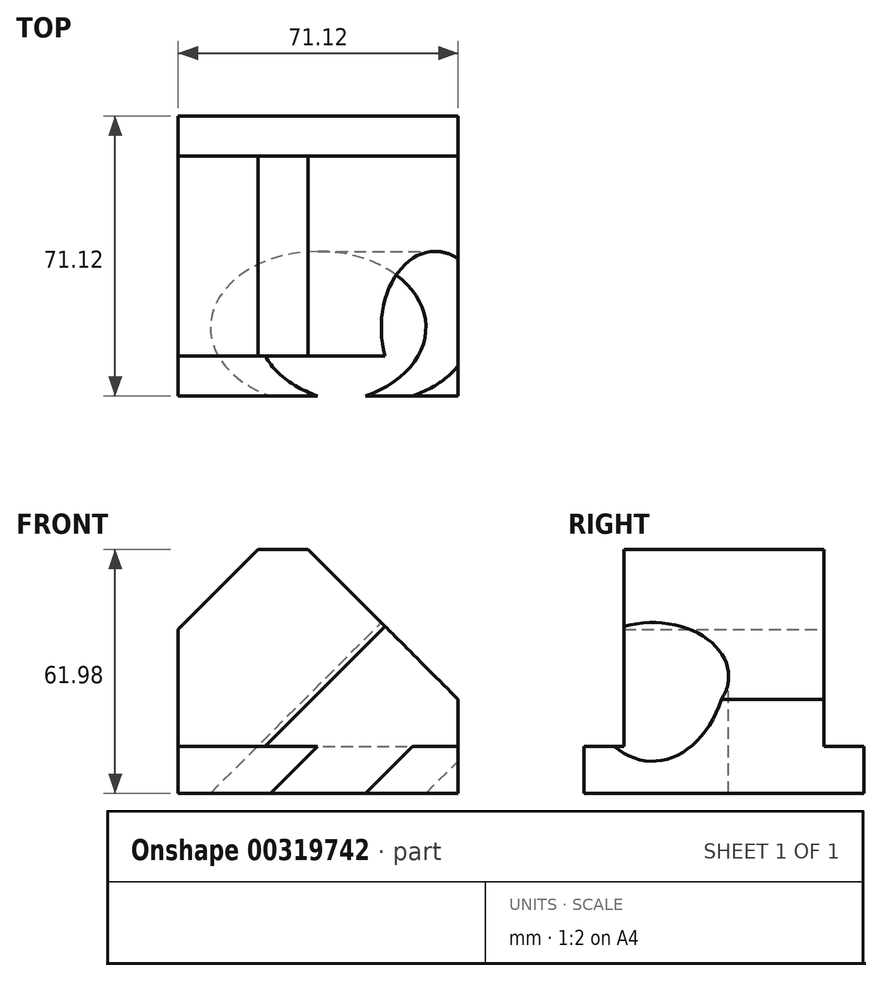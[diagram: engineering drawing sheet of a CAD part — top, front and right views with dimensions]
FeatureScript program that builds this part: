
annotation { "Feature Type Name" : "Feature", "Feature Type Description" : "" }
export const myFeature = defineFeature(function(context is Context, id is Id, definition is map)
    precondition{}
    {
        {
            var Q0;
            Q0=qCreatedBy(makeId("Front.planeOp"),FACE);
            var sketch = newSketch(context, id + "F0", { "sketchPlane" : qUnion([Q0])});
            skLineSegment(sketch, "E0", {"start": v(-35.56, 0) * mm, "end": v(35.56, 0) * mm});
            skLineSegment(sketch, "E1", {"start": v(35.56, 0) * mm, "end": v(35.56, 23.88) * mm});
            skLineSegment(sketch, "E2", {"start": v(35.56, 23.88) * mm, "end": v(-2.54, 61.98) * mm});
            skLineSegment(sketch, "E3", {"start": v(-2.54, 61.98) * mm, "end": v(-15.24, 61.98) * mm});
            skLineSegment(sketch, "E4", {"start": v(-35.56, 0) * mm, "end": v(-35.56, 41.66) * mm});
            skLineSegment(sketch, "E5", {"start": v(-35.56, 41.66) * mm, "end": v(-15.24, 61.98) * mm});
            skSolve(sketch);
        }
        {
            var Q0;
            Q0 = qSketchRegion(id + "F0", true);
            extrude(context, id + "F1", {"entities" : qUnion([Q0]), "endBound" : BoundingType.SYMMETRIC, "depth" : 71.12 * mm});
        }
        {
            var Q0;
            Q0=makeQuery(id+"F1.opExtrude","SWEPT_FACE",FACE,{"disambiguationData":[OSD([sQuery(id+"F0.wireOp",EDGE,"E1")])]});
            var sketch = newSketch(context, id + "F2", { "sketchPlane" : qUnion([Q0])});
            skLineSegment(sketch, "E6.bottom", {"start": v(-35.56, 11.94) * mm, "end": v(-25.4, 11.94) * mm});
            skLineSegment(sketch, "E6.top", {"start": v(-35.56, 61.98) * mm, "end": v(-25.4, 61.98) * mm});
            skLineSegment(sketch, "E6.left", {"start": v(-35.56, 11.94) * mm, "end": v(-35.56, 61.98) * mm});
            skLineSegment(sketch, "E6.right", {"start": v(-25.4, 11.94) * mm, "end": v(-25.4, 61.98) * mm});
            skLineSegment(sketch, "E7.bottom", {"start": v(35.56, 11.94) * mm, "end": v(25.4, 11.94) * mm});
            skLineSegment(sketch, "E7.top", {"start": v(35.56, 61.98) * mm, "end": v(25.4, 61.98) * mm});
            skLineSegment(sketch, "E7.left", {"start": v(35.56, 11.94) * mm, "end": v(35.56, 61.98) * mm});
            skLineSegment(sketch, "E7.right", {"start": v(25.4, 11.94) * mm, "end": v(25.4, 61.98) * mm});
            skSolve(sketch);
        }
        {
            var Q0;
            Q0 = qSketchRegion(id + "F2", true);
            extrude(context, id + "F3", {"entities" : qUnion([Q0]), "operationType" : NewBodyOperationType.REMOVE, "endBound" : BoundingType.THROUGH_ALL, "oppositeDirection" : true, "depth" : 25.4 * mm});
        }
        {
            var Q0;
            Q0=makeQuery(id+"F1.opExtrude","SWEPT_FACE",FACE,{"disambiguationData":[OSD([sQuery(id+"F0.wireOp",EDGE,"E2")])]});
            var sketch = newSketch(context, id + "F4", { "sketchPlane" : qUnion([Q0])});
            skCircle(sketch, "E8", {"center": v(-18.18, 0) * mm, "radius": 19.36 * mm});
            skSolve(sketch);
        }
        {
            var Q0;
            Q0 = qSketchRegion(id + "F4", true);
            extrude(context, id + "F5", {"entities" : qUnion([Q0]), "operationType" : NewBodyOperationType.REMOVE, "endBound" : BoundingType.THROUGH_ALL, "oppositeDirection" : true, "depth" : 25.4 * mm});
        }
    });
